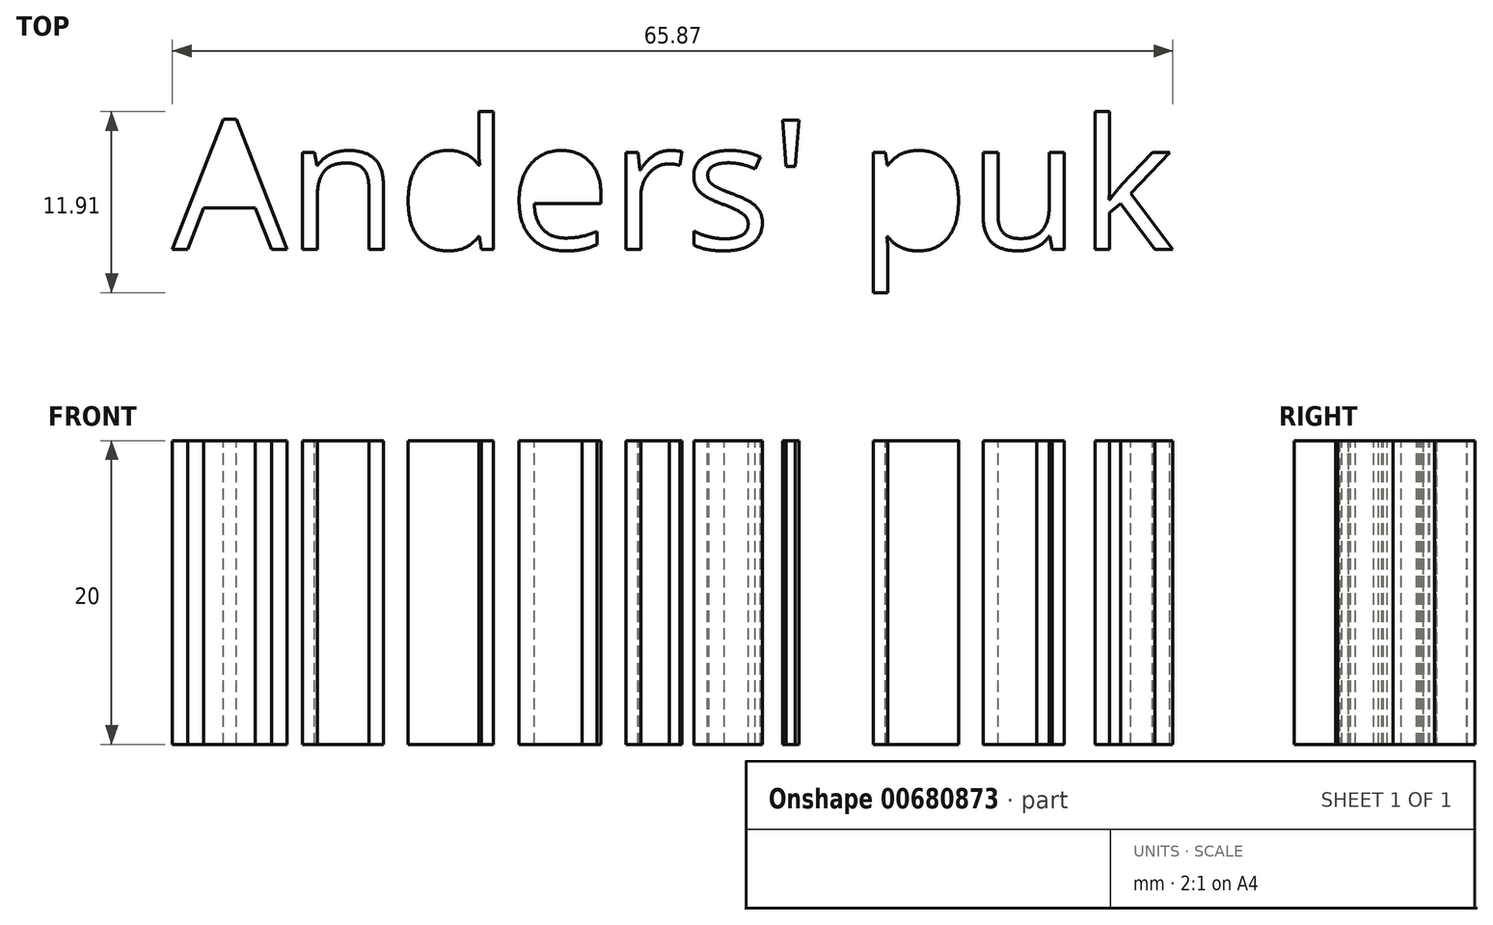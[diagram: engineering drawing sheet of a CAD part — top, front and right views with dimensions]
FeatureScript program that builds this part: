
annotation { "Feature Type Name" : "Feature", "Feature Type Description" : "" }
export const myFeature = defineFeature(function(context is Context, id is Id, definition is map)
    precondition{}
    {
        {
            var Q0;
            Q0=qCreatedBy(makeId("Top.planeOp"),FACE);
            var sketch = newSketch(context, id + "F0", { "sketchPlane" : qUnion([Q0])});
            skCircle(sketch, "E0", {"center": v(0, 0) * mm, "radius": 35 * mm});
            skSolve(sketch);
        }
        {
            var Q0;
            Q0=makeQuery(id+"F0.imprint","IMPRINT",FACE,{"disambiguationData":[TD([[makeQuery(id+"F0.imprint","IMPRINT",EDGE,{"derivedFrom":sQuery(id+"F0.wireOp",EDGE,"E0")}),1.0]])]});
            extrude(context, id + "F1", {"entities" : qUnion([Q0]), "depth" : 20 * mm, "offsetDistance" : 25.4 * mm});
        }
        {
            var Q0;
            Q0=makeQuery(id+"F1.opExtrude","CAP_FACE",FACE,{"disambiguationData":[OSD([sQuery(id+"F0.wireOp",EDGE,"E0")])],"isStart":false});
            var sketch = newSketch(context, id + "F2", { "sketchPlane" : qUnion([Q0])});
            skText(sketch, "E1", { "text": "Anders\' puk", "fontName": "OpenSans-Regular.ttf"});
            const initialGuessF2  = {"E1": [-0.03274, 0, 1, 0, 0.00858]};
            skSetInitialGuess(sketch, initialGuessF2);
            skSolve(sketch);
        }
        {
            var Q0;
            Q0=makeQuery(id+"F2.imprint","IMPRINT",FACE,{"disambiguationData":[TD([[makeQuery(id+"F2.imprint","IMPRINT",EDGE,{"derivedFrom":sQuery(id+"F2.wireOp",EDGE,"E1.sketch_text.stroke-0")}),1.0]])]});
            extrude(context, id + "F3", {"entities" : qUnion([Q0]), "operationType" : NewBodyOperationType.REMOVE, "oppositeDirection" : true, "depth" : 25.4 * mm, "offsetDistance" : 25.4 * mm});
        }
    });
